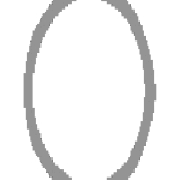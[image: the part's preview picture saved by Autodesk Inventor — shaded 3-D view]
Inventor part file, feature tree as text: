
AUTODESK INVENTOR PART (.ipt)
format: ipt  version: 2021 (Build 250183000, 183)  size: 112,640 bytes
history: native  units: in
note: dims shown in document units (in); Inventor stores cm internally (conversion verified against a paired STEP export)
features: other x4, sketch x3, plane x1
ambient origin geometry x8: Origin, YZ Plane, XZ Plane, XY Plane, X Axis, Y Axis, Z Axis, Center Point
bodies: Solid1 (feature_tree), Body (feature_tree)
feature tree (8):
  other  "Driven Length"
  other  "Frame Generator"
  other  "Start Plane"
  other  "End Plane"
  sketch  "Sketch"  dims[d2=16.0833in d4=-0.0in d5=16.0833in d6=0.12in d7=0.0in d8=90.0deg d9=16.0833in]
  sketch  "Sketch2"  dims[d0=1.0in]
  plane  "Work Plane3"
  sketch  "Sketch3"  dims[d1=0.065in]
